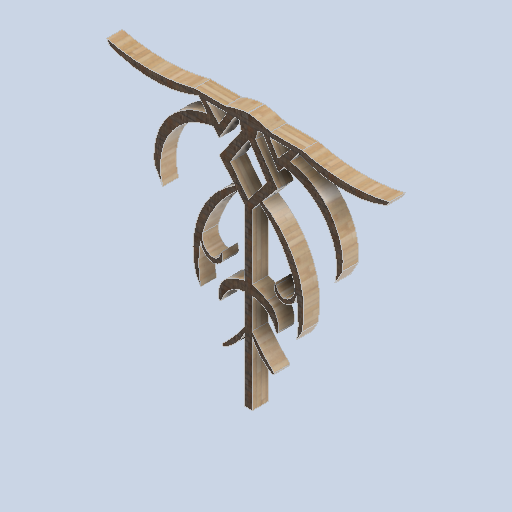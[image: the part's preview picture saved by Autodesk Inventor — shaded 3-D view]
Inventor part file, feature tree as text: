
AUTODESK INVENTOR PART (.ipt)
format: ipt  version: 2024.2 (Build 282272000, 272)  size: 330,752 bytes
history: native  units: in
note: dims shown in document units (in); Inventor stores cm internally (conversion verified against a paired STEP export)
features: other x3, sketch x3
ambient origin geometry x8: Origin, YZ Plane, XZ Plane, XY Plane, X Axis, Y Axis, Z Axis, Center Point
bodies: Solid1 (feature_tree)
feature tree (6):
  other  "side_art_frame_01.ipt"
  other  "Solid1::side_art_frame_01.ipt"
  other  "TaggingFeature1"
  sketch  "Sketch1"  dims[d0=0.3937in]
  sketch  "Sketch2"
  sketch  "Sketch3"
